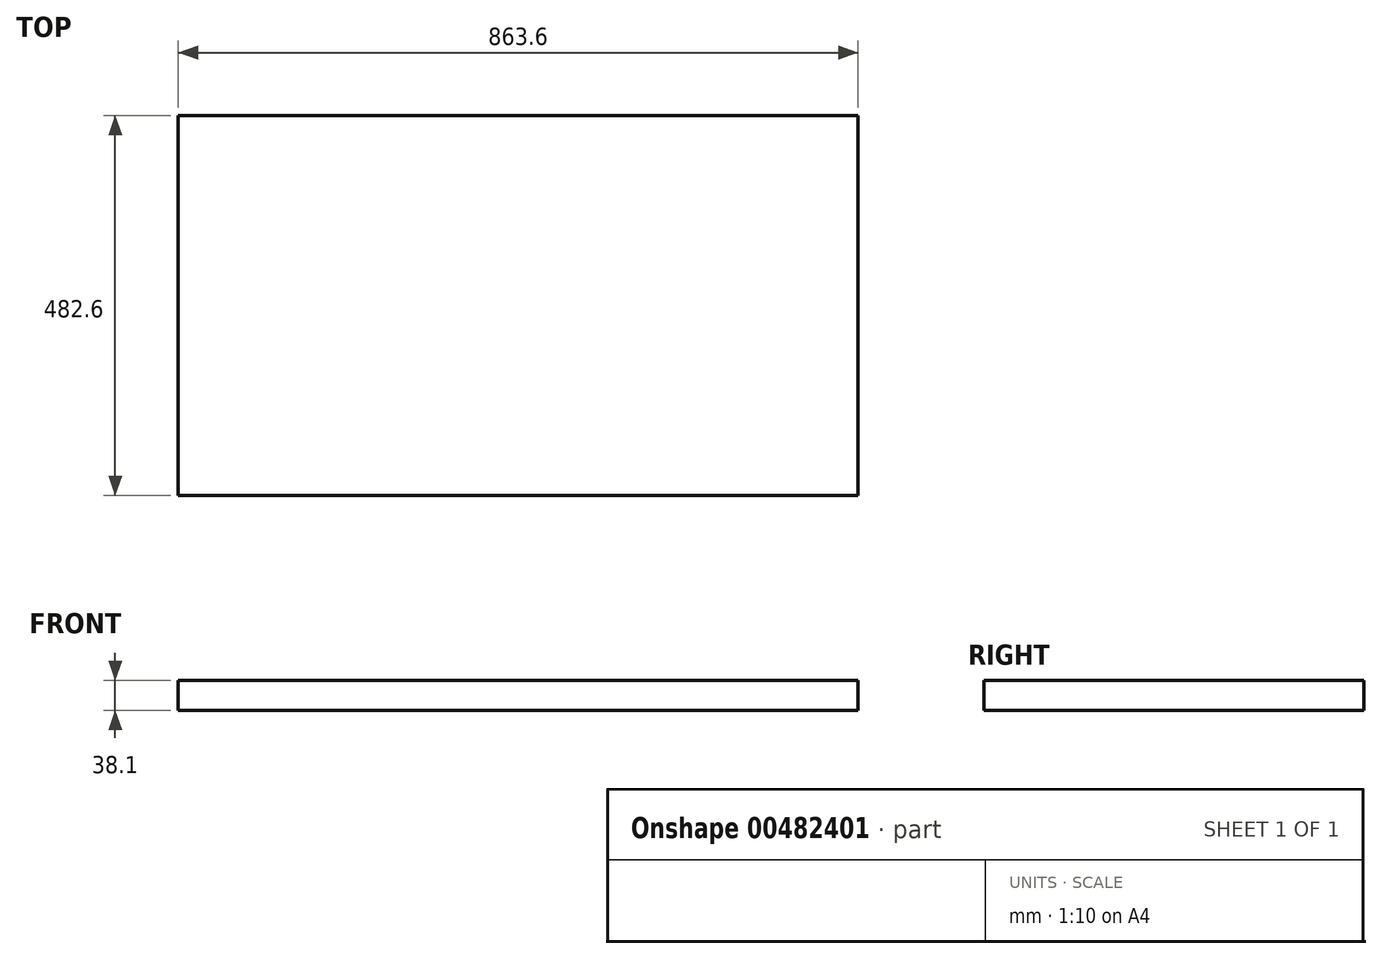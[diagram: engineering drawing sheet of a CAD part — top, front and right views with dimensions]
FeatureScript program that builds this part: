
annotation { "Feature Type Name" : "Feature", "Feature Type Description" : "" }
export const myFeature = defineFeature(function(context is Context, id is Id, definition is map)
    precondition{}
    {
        {
            var Q0;
            Q0=qCreatedBy(makeId("Top.planeOp"),FACE);
            var sketch = newSketch(context, id + "F0", { "sketchPlane" : qUnion([Q0])});
            skLineSegment(sketch, "E0.bottom", {"start": v(431.8, -241.3) * mm, "end": v(-431.8, -241.3) * mm});
            skLineSegment(sketch, "E0.top", {"start": v(431.8, 241.3) * mm, "end": v(-431.8, 241.3) * mm});
            skLineSegment(sketch, "E0.left", {"start": v(431.8, -241.3) * mm, "end": v(431.8, 241.3) * mm});
            skLineSegment(sketch, "E0.right", {"start": v(-431.8, -241.3) * mm, "end": v(-431.8, 241.3) * mm});
            skPoint(sketch, "E0.middle", {"position": v(0, 0) * mm});
            skSolve(sketch);
        }
        {
            var Q0;
            Q0 = qSketchRegion(id + "F0", true);
            extrude(context, id + "F1", {"entities" : qUnion([Q0]), "depth" : 38.1 * mm, "offsetDistance" : 25.4 * mm});
        }
    });
